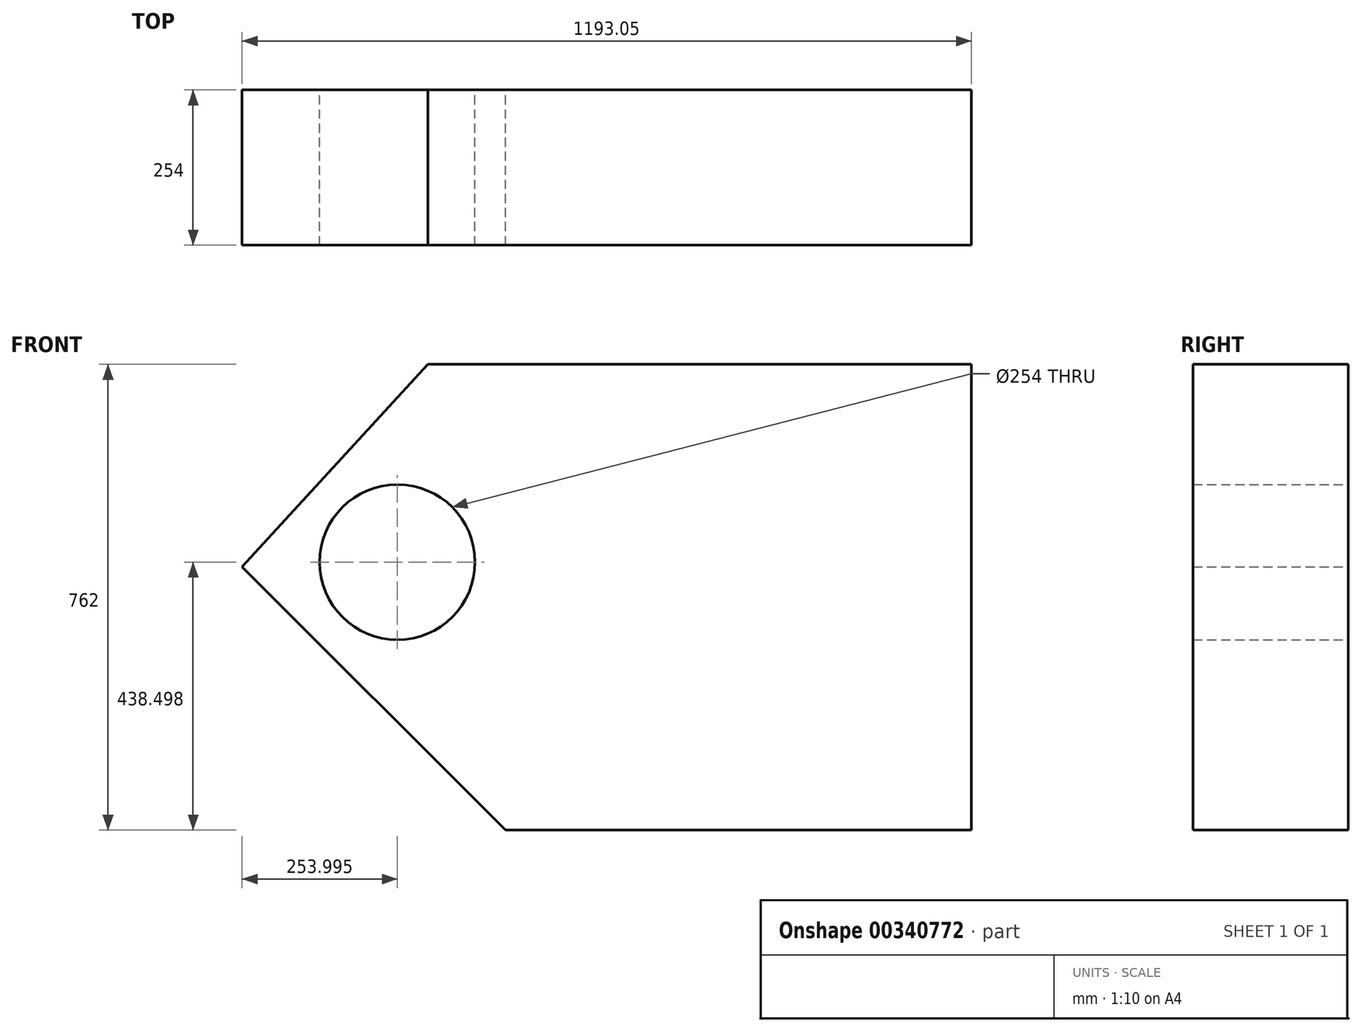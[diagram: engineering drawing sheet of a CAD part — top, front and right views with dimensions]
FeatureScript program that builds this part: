
annotation { "Feature Type Name" : "Feature", "Feature Type Description" : "" }
export const myFeature = defineFeature(function(context is Context, id is Id, definition is map)
    precondition{}
    {
        {
            var Q0;
            Q0=qCreatedBy(makeId("Front.planeOp"),FACE);
            var sketch = newSketch(context, id + "F0", { "sketchPlane" : qUnion([Q0])});
            skLineSegment(sketch, "E0", {"start": v(-468.77, 70.5) * mm, "end": v(420.23, 70.5) * mm});
            skLineSegment(sketch, "E1", {"start": v(420.23, 70.5) * mm, "end": v(420.23, -691.5) * mm});
            skLineSegment(sketch, "E2", {"start": v(420.23, -691.5) * mm, "end": v(-341.77, -691.5) * mm});
            skLineSegment(sketch, "E3", {"start": v(-341.77, -691.5) * mm, "end": v(-772.82, -260.44) * mm});
            skCircle(sketch, "E4", {"center": v(-518.82, -253) * mm, "radius": 127 * mm});
            skLineSegment(sketch, "E5", {"start": v(-772.82, -260.44) * mm, "end": v(-468.77, 70.5) * mm});
            skSolve(sketch);
        }
        {
            var Q0;
            Q0 = qSketchRegion(id + "F0", true);
            extrude(context, id + "F1", {"entities" : qUnion([Q0]), "depth" : 254 * mm});
        }
    });
